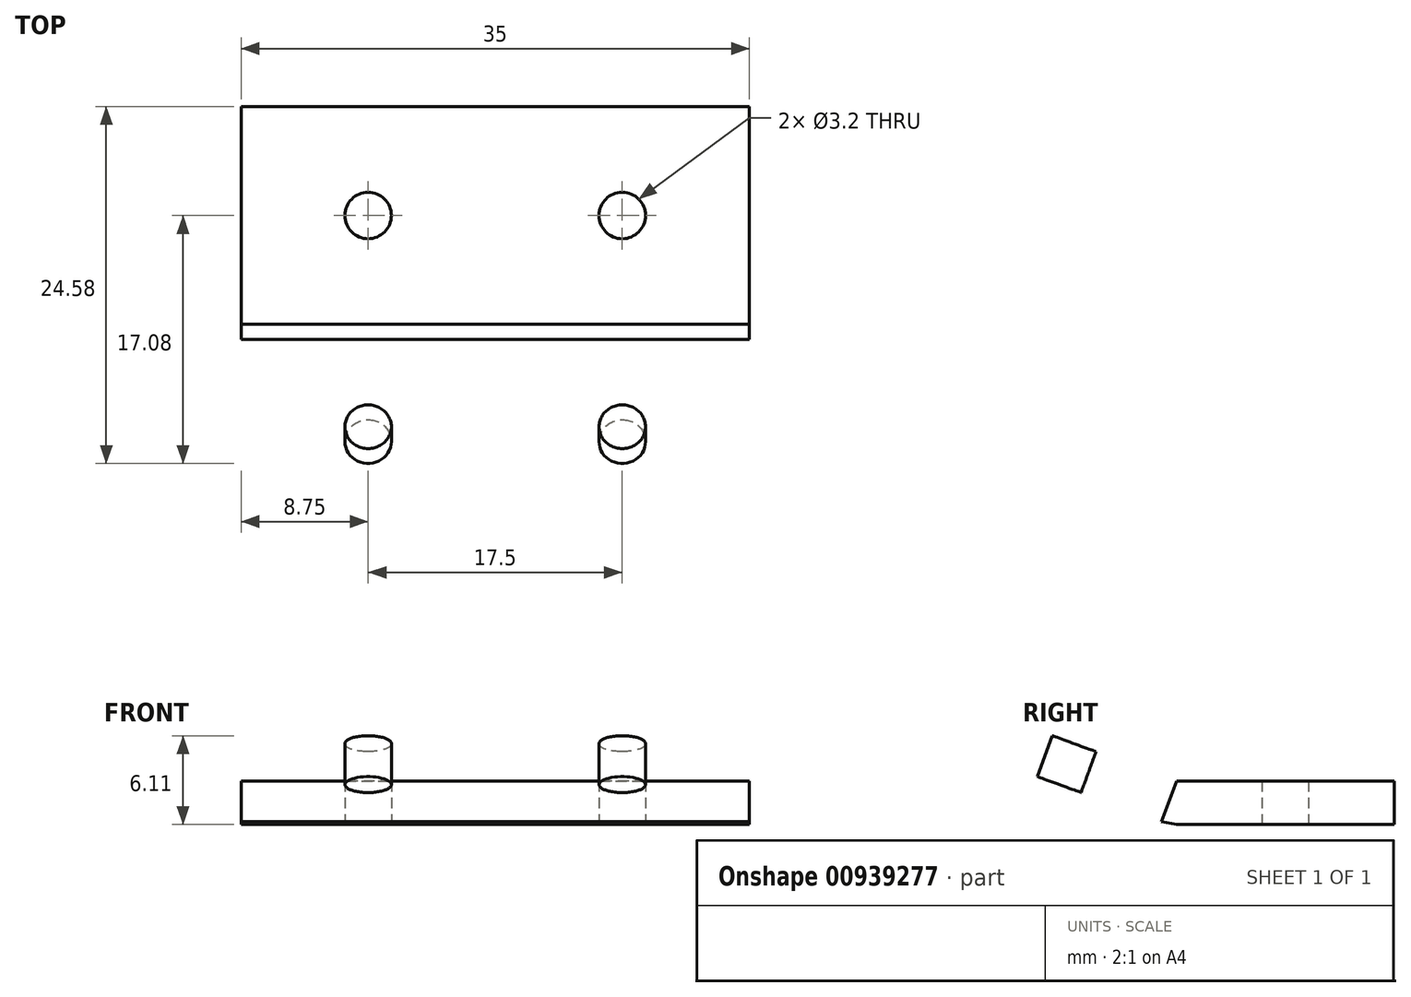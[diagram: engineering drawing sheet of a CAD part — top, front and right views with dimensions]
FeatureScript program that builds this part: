
annotation { "Feature Type Name" : "Feature", "Feature Type Description" : "" }
export const myFeature = defineFeature(function(context is Context, id is Id, definition is map)
    precondition{}
    {
        {
            var Q0;
            Q0=qCreatedBy(makeId("Top.planeOp"),FACE);
            var sketch = newSketch(context, id + "F0", { "sketchPlane" : qUnion([Q0])});
            skLineSegment(sketch, "E0.bottom", {"start": v(-17.5, -7.5) * mm, "end": v(17.5, -7.5) * mm});
            skLineSegment(sketch, "E0.top", {"start": v(-17.5, 7.5) * mm, "end": v(17.5, 7.5) * mm});
            skLineSegment(sketch, "E0.left", {"start": v(-17.5, -7.5) * mm, "end": v(-17.5, 7.5) * mm});
            skLineSegment(sketch, "E0.right", {"start": v(17.5, -7.5) * mm, "end": v(17.5, 7.5) * mm});
            skPoint(sketch, "E0.middle", {"position": v(0, 0) * mm});
            skLineSegment(sketch, "E1", {"start": v(0, 0) * mm, "end": v(-17.5, 0) * mm});
            skLineSegment(sketch, "E2", {"start": v(0, 0) * mm, "end": v(17.5, 0) * mm});
            skCircle(sketch, "E3", {"center": v(-8.75, 0) * mm, "radius": 1.6 * mm});
            skCircle(sketch, "E4", {"center": v(8.75, 0) * mm, "radius": 1.6 * mm});
            skSolve(sketch);
        }
        {
            var Q0;
            {var subQ6=sQuery(id+"F0.wireOp",EDGE,"E0.bottom");Q0=makeQuery(id+"F0.imprint","IMPRINT",FACE,{"disambiguationData":[TD([[makeQuery(id+"F0.imprint","IMPRINT",EDGE,{"derivedFrom":subQ6}),1.0]])]});}
            var Q1;
            {var subQ1=sQuery(id+"F0.wireOp",EDGE,"E0.top");Q1=makeQuery(id+"F0.imprint","IMPRINT",FACE,{"disambiguationData":[TD([[makeQuery(id+"F0.imprint","IMPRINT",EDGE,{"derivedFrom":subQ1}),-1.0]])]});}
            extrude(context, id + "F1", {"entities" : qUnion([Q0, Q1]), "depth" : 3 * mm, "offsetDistance" : 25 * mm});
        }
        {
            var Q0;
            Q0=makeQuery(id+"F1.opExtrude","SWEPT_FACE",FACE,{"disambiguationData":[OSD([sQuery(id+"F0.wireOp",EDGE,"E0.right")])]});
            var sketch = newSketch(context, id + "F2", { "sketchPlane" : qUnion([Q0])});
            skLineSegment(sketch, "E5", {"start": v(-7.5, 3) * mm, "end": v(-21.6, 8.13) * mm});
            skLineSegment(sketch, "E6", {"start": v(-21.6, 8.13) * mm, "end": v(-22.62, 5.31) * mm});
            skLineSegment(sketch, "E7", {"start": v(-22.62, 5.31) * mm, "end": v(-8.53, 0.18) * mm});
            skLineSegment(sketch, "E8", {"start": v(-8.53, 0.18) * mm, "end": v(-7.5, 3) * mm});
            skLineSegment(sketch, "E9", {"start": v(-8.53, 0.18) * mm, "end": v(-7.5, 0) * mm});
            skSolve(sketch);
        }
        {
            var Q0;
            Q0 = qSketchRegion(id + "F2", true);
            var Q1;
            Q1=makeQuery(id+"F2.imprint","IMPRINT",FACE,{"disambiguationData":[TD([[makeQuery(id+"F2.imprint","IMPRINT",EDGE,{"derivedFrom":sQuery(id+"F2.wireOp",EDGE,"E8")}),-1.0]])]});
            extrude(context, id + "F3", {"entities" : qUnion([Q0, Q1]), "operationType" : NewBodyOperationType.ADD, "oppositeDirection" : true, "depth" : 35 * mm, "offsetDistance" : 25 * mm});
        }
        {
            var Q0;
            Q0=makeQuery(id+"F3.opExtrude","SWEPT_FACE",FACE,{"disambiguationData":[OSD([sQuery(id+"F2.wireOp",EDGE,"E7")])]});
            var sketch = newSketch(context, id + "F4", { "sketchPlane" : qUnion([Q0])});
            skLineSegment(sketch, "E10", {"start": v(0, 23.07) * mm, "end": v(0, 8.07) * mm});
            skLineSegment(sketch, "E11", {"start": v(0, 15.57) * mm, "end": v(17.5, 15.57) * mm});
            skLineSegment(sketch, "E12", {"start": v(0, 15.57) * mm, "end": v(-17.5, 15.57) * mm});
            skCircle(sketch, "E13", {"center": v(8.75, 15.57) * mm, "radius": 1.6 * mm});
            skCircle(sketch, "E14", {"center": v(-8.75, 15.57) * mm, "radius": 1.6 * mm});
            skSolve(sketch);
        }
        {
            var Q0;
            {var subQ0=sQuery(id+"F4.wireOp",EDGE,"E13");var subQ1=sQuery(id+"F4.wireOp",EDGE,"E11");var subQ2=makeQuery(id+"F4.imprint","INTERSECT",VERTEX,{"disambiguationData":[OD(0.0)],"derivedFrom":[subQ1,subQ0]});Q0=makeQuery(id+"F4.imprint","IMPRINT",FACE,{"disambiguationData":[TD([[makeQuery(id+"F4.imprint","IMPRINT",EDGE,{"disambiguationData":[TD([[subQ2,-1.0]])],"derivedFrom":subQ1}),-1.0]])]});}
            var Q1;
            {var subQ0=sQuery(id+"F4.wireOp",EDGE,"E13");var subQ1=sQuery(id+"F4.wireOp",EDGE,"E11");var subQ2=makeQuery(id+"F4.imprint","INTERSECT",VERTEX,{"disambiguationData":[OD(0.0)],"derivedFrom":[subQ1,subQ0]});Q1=makeQuery(id+"F4.imprint","IMPRINT",FACE,{"disambiguationData":[TD([[makeQuery(id+"F4.imprint","IMPRINT",EDGE,{"disambiguationData":[TD([[subQ2,-1.0]])],"derivedFrom":subQ1}),1.0]])]});}
            var Q2;
            {var subQ0=sQuery(id+"F4.wireOp",EDGE,"E14");var subQ1=sQuery(id+"F4.wireOp",EDGE,"E12");var subQ2=makeQuery(id+"F4.imprint","INTERSECT",VERTEX,{"disambiguationData":[OD(0.0)],"derivedFrom":[subQ1,subQ0]});Q2=makeQuery(id+"F4.imprint","IMPRINT",FACE,{"disambiguationData":[TD([[makeQuery(id+"F4.imprint","IMPRINT",EDGE,{"disambiguationData":[TD([[subQ2,-1.0]])],"derivedFrom":subQ1}),-1.0]])]});}
            var Q3;
            {var subQ0=sQuery(id+"F4.wireOp",EDGE,"E14");var subQ1=sQuery(id+"F4.wireOp",EDGE,"E12");var subQ2=makeQuery(id+"F4.imprint","INTERSECT",VERTEX,{"disambiguationData":[OD(0.0)],"derivedFrom":[subQ1,subQ0]});Q3=makeQuery(id+"F4.imprint","IMPRINT",FACE,{"disambiguationData":[TD([[makeQuery(id+"F4.imprint","IMPRINT",EDGE,{"disambiguationData":[TD([[subQ2,-1.0]])],"derivedFrom":subQ1}),1.0]])]});}
            extrude(context, id + "F5", {"entities" : qUnion([Q0, Q1, Q2, Q3]), "operationType" : NewBodyOperationType.REMOVE, "oppositeDirection" : true, "depth" : 25 * mm, "offsetDistance" : 25 * mm});
        }
    });
